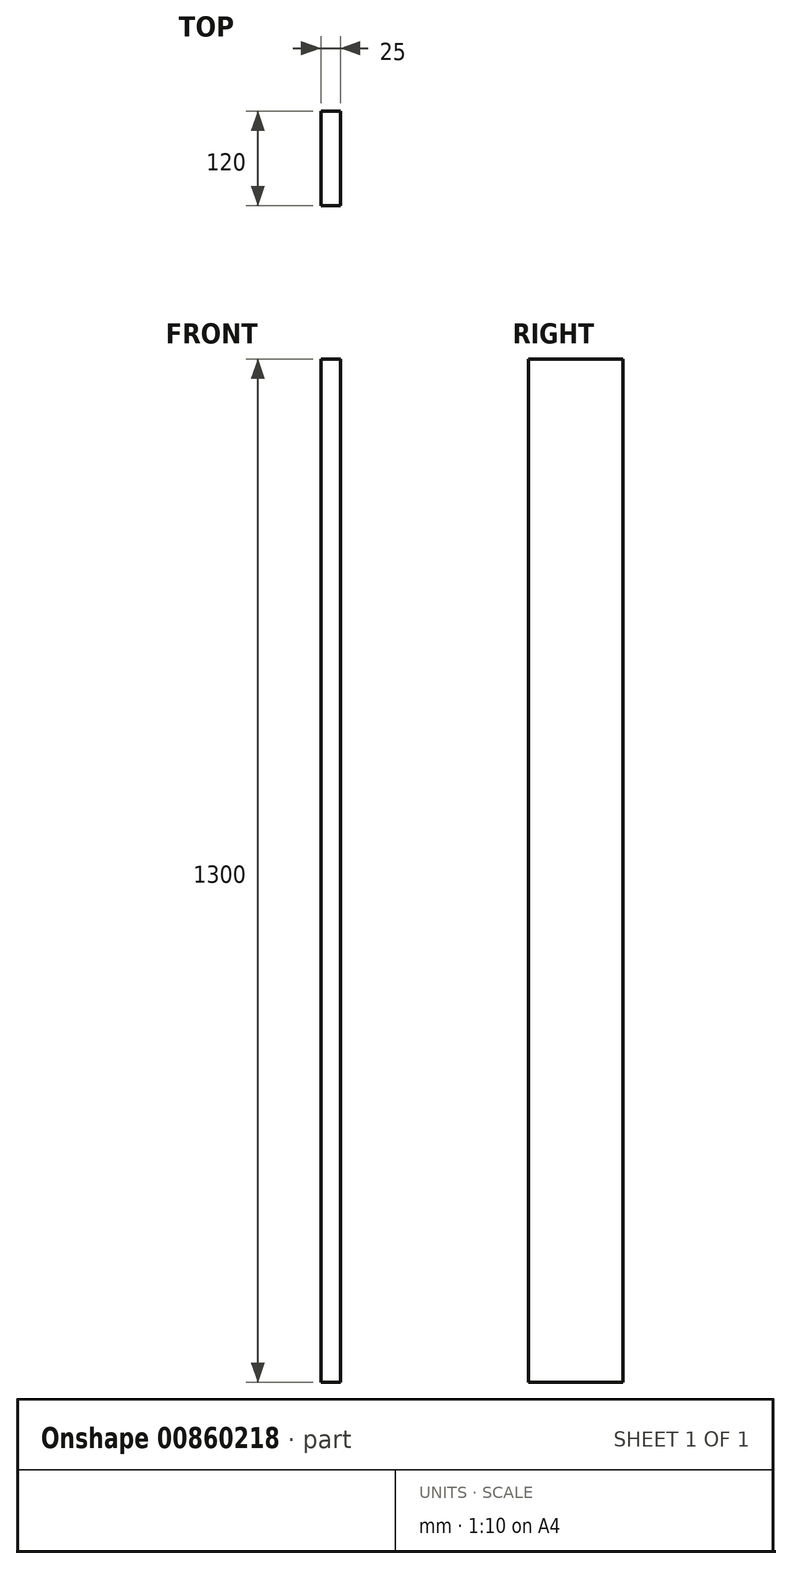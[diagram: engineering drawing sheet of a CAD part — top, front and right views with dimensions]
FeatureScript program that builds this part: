
annotation { "Feature Type Name" : "Feature", "Feature Type Description" : "" }
export const myFeature = defineFeature(function(context is Context, id is Id, definition is map)
    precondition{}
    {
        {
            var Q0;
            Q0=qCreatedBy(makeId("Right.planeOp"),FACE);
            var sketch = newSketch(context, id + "F0", { "sketchPlane" : qUnion([Q0])});
            skLineSegment(sketch, "E0.bottom", {"start": v(0, 0) * mm, "end": v(120, 0) * mm});
            skLineSegment(sketch, "E0.top", {"start": v(0, 1300) * mm, "end": v(120, 1300) * mm});
            skLineSegment(sketch, "E0.left", {"start": v(0, 0) * mm, "end": v(0, 1300) * mm});
            skLineSegment(sketch, "E0.right", {"start": v(120, 0) * mm, "end": v(120, 1300) * mm});
            skSolve(sketch);
        }
        {
            var Q0;
            Q0=makeQuery(id+"F0.imprint","IMPRINT",FACE,{"disambiguationData":[TD([[makeQuery(id+"F0.imprint","IMPRINT",EDGE,{"derivedFrom":sQuery(id+"F0.wireOp",EDGE,"E0.bottom")}),1.0]])]});
            extrude(context, id + "F1", {"entities" : qUnion([Q0]), "depth" : 25 * mm, "offsetDistance" : 25 * mm});
        }
    });
